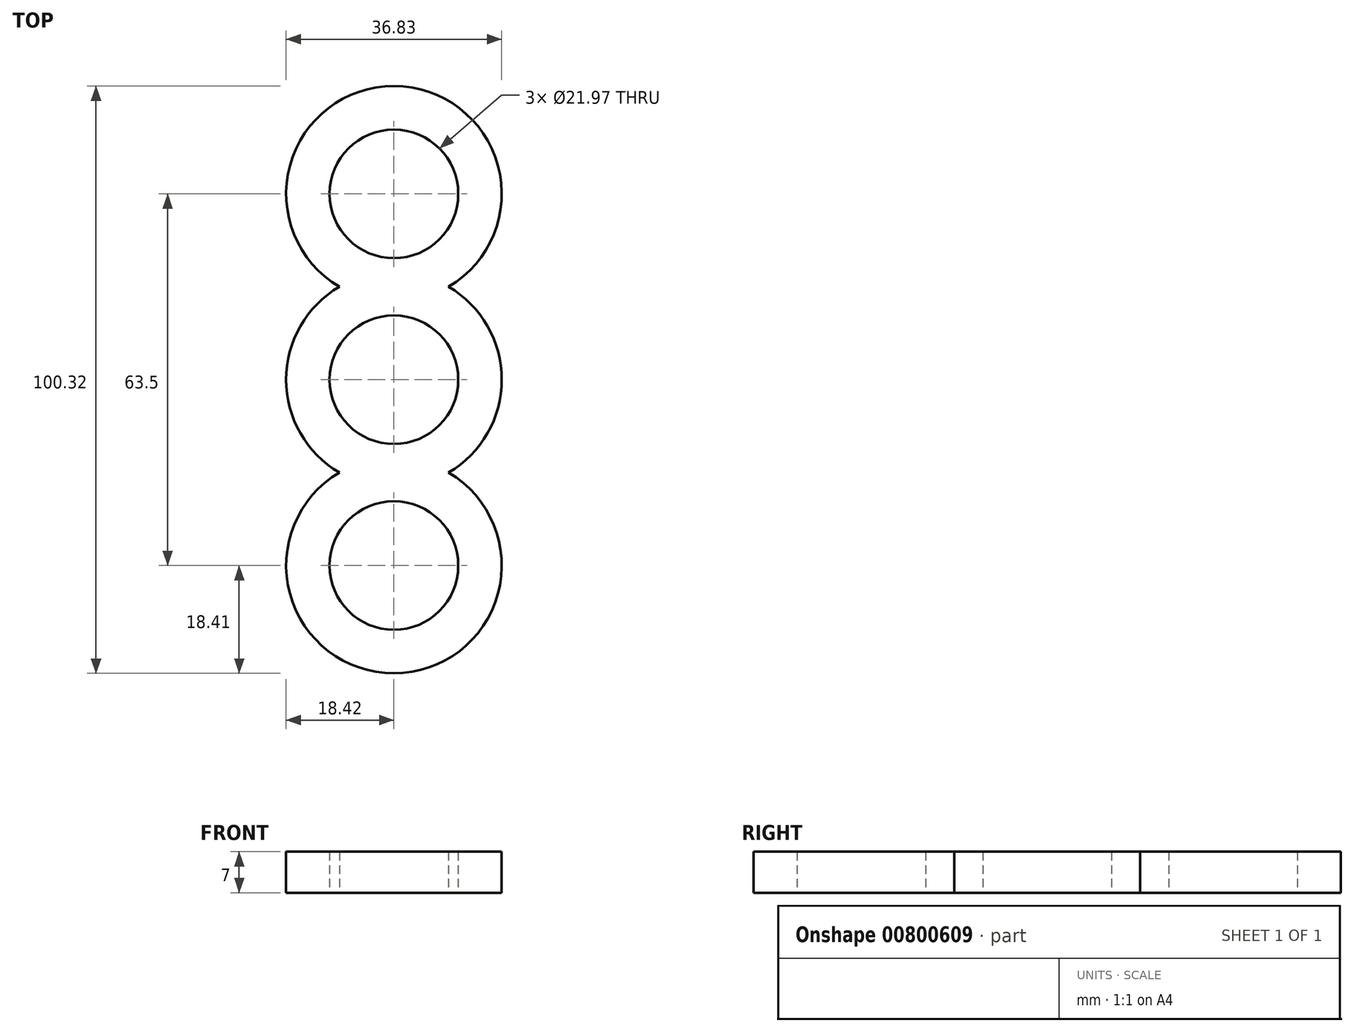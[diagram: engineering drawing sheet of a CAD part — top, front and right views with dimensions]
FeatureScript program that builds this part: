
annotation { "Feature Type Name" : "Feature", "Feature Type Description" : "" }
export const myFeature = defineFeature(function(context is Context, id is Id, definition is map)
    precondition{}
    {
        {
            var Q0;
            Q0=qCreatedBy(makeId("Top.planeOp"),FACE);
            var sketch = newSketch(context, id + "F0", { "sketchPlane" : qUnion([Q0])});
            skCircle(sketch, "E0", {"center": v(0, 0) * mm, "radius": 10.99 * mm});
            skCircle(sketch, "E1", {"center": v(0, 31.75) * mm, "radius": 10.99 * mm});
            skCircle(sketch, "E2", {"center": v(0, -31.75) * mm, "radius": 10.99 * mm});
            skLineSegment(sketch, "E3", {"start": v(0, 31.75) * mm, "end": v(0, -31.75) * mm, "construction": true});
            skArc(sketch, "E4", {"start": v(9.33, 15.88) * mm, "mid": v(0, 50.16) * mm, "end": v(-9.33, 15.88) * mm});
            skArc(sketch, "E5", {"start": v(-9.33, -15.88) * mm, "mid": v(0, -50.16) * mm, "end": v(9.33, -15.87) * mm});
            skArc(sketch, "E6", {"start": v(-9.33, 15.87) * mm, "mid": v(-18.41, 0) * mm, "end": v(-9.33, -15.88) * mm});
            skArc(sketch, "E7.trimOffspring", {"start": v(9.33, -15.87) * mm, "mid": v(18.41, 0) * mm, "end": v(9.33, 15.88) * mm});
            skSolve(sketch);
        }
        {
            var Q0;
            Q0 = qSketchRegion(id + "F0", true);
            extrude(context, id + "F1", {"entities" : qUnion([Q0]), "depth" : 7 * mm, "offsetDistance" : 25.4 * mm});
        }
    });
